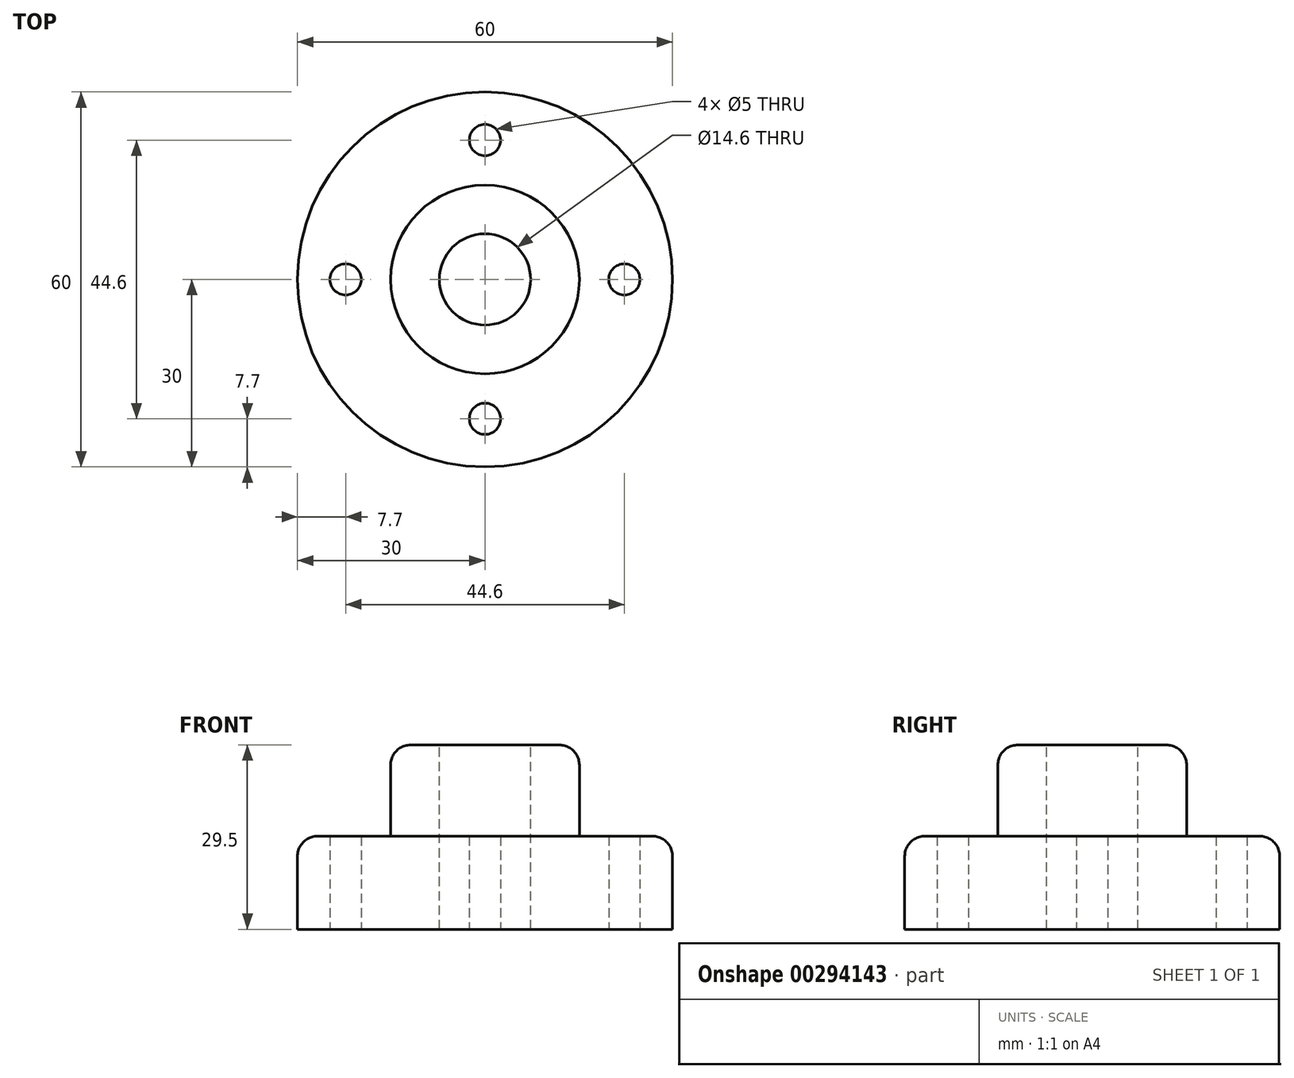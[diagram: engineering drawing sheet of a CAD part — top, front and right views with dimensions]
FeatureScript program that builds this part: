
annotation { "Feature Type Name" : "Feature", "Feature Type Description" : "" }
export const myFeature = defineFeature(function(context is Context, id is Id, definition is map)
    precondition{}
    {
        {
            var Q0;
            Q0=qCreatedBy(makeId("Top.planeOp"),FACE);
            var sketch = newSketch(context, id + "F0", { "sketchPlane" : qUnion([Q0])});
            skCircle(sketch, "E0", {"center": v(0, 0) * mm, "radius": 30 * mm});
            skPoint(sketch, "E1", {"position": v(0, -22.3) * mm});
            skPoint(sketch, "E2", {"position": v(22.3, 0) * mm});
            skPoint(sketch, "E3", {"position": v(-22.3, 0) * mm});
            skPoint(sketch, "E4", {"position": v(0, 22.3) * mm});
            skCircle(sketch, "E5", {"center": v(22.3, 0) * mm, "radius": 2.5 * mm});
            skCircle(sketch, "E6", {"center": v(0, 22.3) * mm, "radius": 2.5 * mm});
            skCircle(sketch, "E7", {"center": v(-22.3, 0) * mm, "radius": 2.5 * mm});
            skCircle(sketch, "E8", {"center": v(0, -22.3) * mm, "radius": 2.5 * mm});
            skSolve(sketch);
        }
        {
            var Q0;
            Q0 = qSketchRegion(id + "F0", true);
            extrude(context, id + "F1", {"entities" : qUnion([Q0]), "depth" : 14.9 * mm});
        }
        {
            var Q0;
            Q0=makeQuery(id+"F1.opExtrude","CAP_EDGE",EDGE,{"disambiguationData":[OSD([sQuery(id+"F0.wireOp",EDGE,"E0")])],"isStart":false});
            fillet(context, id + "F2", {"entities" : qUnion([Q0]), "radius" : 3.2 * mm, "tangentPropagation" : true, "allowEdgeOverflow" : false});
        }
        {
            var Q0;
            Q0=makeQuery(id+"F1.opExtrude","CAP_FACE",FACE,{"disambiguationData":[OSD([sQuery(id+"F0.wireOp",EDGE,"E0"),sQuery(id+"F0.wireOp",EDGE,"E5"),sQuery(id+"F0.wireOp",EDGE,"E6"),sQuery(id+"F0.wireOp",EDGE,"E7"),sQuery(id+"F0.wireOp",EDGE,"E8")])],"isStart":false});
            var sketch = newSketch(context, id + "F3", { "sketchPlane" : qUnion([Q0])});
            skCircle(sketch, "E9", {"center": v(0, 0) * mm, "radius": 15.1 * mm});
            skSolve(sketch);
        }
        {
            var Q0;
            Q0 = qSketchRegion(id + "F3", true);
            extrude(context, id + "F4", {"entities" : qUnion([Q0]), "operationType" : NewBodyOperationType.ADD, "depth" : 14.6 * mm});
        }
        {
            var Q0;
            Q0=makeQuery(id+"F4.opExtrude","CAP_EDGE",EDGE,{"disambiguationData":[OSD([sQuery(id+"F3.wireOp",EDGE,"E9")])],"isStart":false});
            fillet(context, id + "F5", {"entities" : qUnion([Q0]), "radius" : 3.2 * mm, "tangentPropagation" : true, "allowEdgeOverflow" : false});
        }
        {
            var Q0;
            Q0=makeQuery(id+"F4.opExtrude","CAP_FACE",FACE,{"disambiguationData":[OSD([sQuery(id+"F3.wireOp",EDGE,"E9")])],"isStart":false});
            var sketch = newSketch(context, id + "F6", { "sketchPlane" : qUnion([Q0])});
            skCircle(sketch, "E10", {"center": v(0, 0) * mm, "radius": 7.3 * mm});
            skSolve(sketch);
        }
        {
            var Q0;
            Q0 = qSketchRegion(id + "F6", true);
            extrude(context, id + "F7", {"entities" : qUnion([Q0]), "operationType" : NewBodyOperationType.REMOVE, "oppositeDirection" : true, "depth" : 60 * mm});
        }
    });
